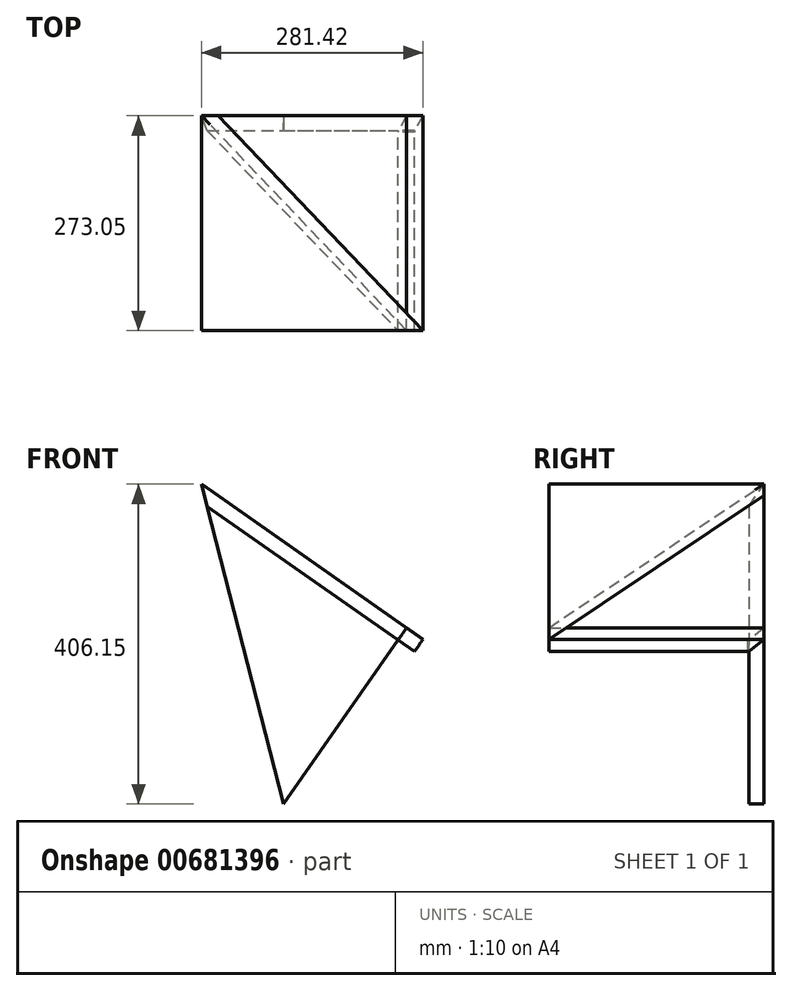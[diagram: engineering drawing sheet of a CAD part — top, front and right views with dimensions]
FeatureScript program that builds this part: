
annotation { "Feature Type Name" : "Feature", "Feature Type Description" : "" }
export const myFeature = defineFeature(function(context is Context, id is Id, definition is map)
    precondition{}
    {
        {
            var Q0;
            Q0=qCreatedBy(makeId("Front.planeOp"),FACE);
            var sketch = newSketch(context, id + "F0", { "sketchPlane" : qUnion([Q0])});
            skLineSegment(sketch, "E0", {"start": v(0, 0) * mm, "end": v(249.68, -174.83) * mm});
            skLineSegment(sketch, "E1", {"start": v(0, 0) * mm, "end": v(0, -53.72) * mm});
            skLineSegment(sketch, "E2", {"start": v(10.93, 15.6) * mm, "end": v(260.6, -159.22) * mm});
            skLineSegment(sketch, "E3", {"start": v(260.6, -159.22) * mm, "end": v(249.68, -174.83) * mm});
            skLineSegment(sketch, "E4", {"start": v(0, 0) * mm, "end": v(0, 29.97) * mm});
            skLineSegment(sketch, "E5", {"start": v(10.93, 15.6) * mm, "end": v(0, 23.26) * mm});
            skSolve(sketch);
        }
        {
            var Q0;
            Q0=makeQuery(id+"F0.imprint","IMPRINT",FACE,{"disambiguationData":[TD([[makeQuery(id+"F0.imprint","IMPRINT",EDGE,{"derivedFrom":sQuery(id+"F0.wireOp",EDGE,"E0")}),1.0]])]});
            extrude(context, id + "F1", {"entities" : qUnion([Q0]), "depth" : 273.05 * mm, "offsetDistance" : 25.4 * mm});
        }
        {
            var Q0;
            Q0=makeQuery(id+"F1.opExtrude","SWEPT_FACE",FACE,{"disambiguationData":[OSD([sQuery(id+"F0.wireOp",EDGE,"E2")])]});
            var sketch = newSketch(context, id + "F2", { "sketchPlane" : qUnion([Q0])});
            skPoint(sketch, "E6.startSnap0", {"position": v(304.8, -136.53) * mm});
            skLineSegment(sketch, "E7", {"start": v(304.8, 0) * mm, "end": v(304.8, 0) * mm});
            skLineSegment(sketch, "E8", {"start": v(304.8, -273.05) * mm, "end": v(-13.34, -273.05) * mm});
            skLineSegment(sketch, "E9", {"start": v(-13.34, -273.05) * mm, "end": v(-13.34, -88.9) * mm});
            skLineSegment(sketch, "E10", {"start": v(-13.34, -88.9) * mm, "end": v(-13.34, 0) * mm});
            skLineSegment(sketch, "E11", {"start": v(-13.34, 0) * mm, "end": v(304.8, -273.05) * mm});
            skSolve(sketch);
        }
        {
            var Q0;
            Q0 = qSketchRegion(id + "F2", true);
            extrude(context, id + "F3", {"entities" : qUnion([Q0]), "operationType" : NewBodyOperationType.REMOVE, "oppositeDirection" : true, "depth" : 25.4 * mm, "offsetDistance" : 25.4 * mm});
        }
        {
            var Q0;
            Q0=makeQuery(id+"F3.boolean.opBoolean","INTERSECT",EDGE,{"derivedFrom":[makeQuery(id+"F1.opExtrude","SWEPT_FACE",FACE,{"disambiguationData":[OSD([sQuery(id+"F0.wireOp",EDGE,"E0")])]}),makeQuery(id+"F3.opExtrude","SWEPT_FACE",FACE,{"disambiguationData":[OSD([sQuery(id+"F2.wireOp",EDGE,"XtUcBT52-hiCQ-KWcL-Mt3B-IRJ0phNK8BbC")])]})]});
            var Q1;
            Q1=makeQuery(id+"F3.boolean.opBoolean","INTERSECT",EDGE,{"derivedFrom":[makeQuery(id+"F1.opExtrude","SWEPT_FACE",FACE,{"disambiguationData":[OSD([sQuery(id+"F0.wireOp",EDGE,"E0")])]}),makeQuery(id+"F3.opExtrude","SWEPT_FACE",FACE,{"disambiguationData":[OSD([sQuery(id+"F2.wireOp",EDGE,"sxALio6w-iuIC-QzVB-jW2B-1LGJXtkoLwBy")])]})]});
            var Q2;
            Q2=makeQuery(id+"F1.opExtrude","CAP_EDGE",EDGE,{"disambiguationData":[OSD([sQuery(id+"F0.wireOp",EDGE,"E0")])],"isStart":true});
            chamfer(context, id + "F4", {"entities" : qUnion([Q0, Q1, Q2]), "width" : 19.05 * mm, "tangentPropagation" : true});
        }
        {
            var Q0;
            Q0=makeQuery(id+"F1.opExtrude","SWEPT_BODY",BODY,{"disambiguationData":[OSD([sQuery(id+"F0.wireOp",EDGE,"E0"),sQuery(id+"F0.wireOp",EDGE,"E2"),sQuery(id+"F0.wireOp",EDGE,"E3"),sQuery(id+"F0.wireOp",EDGE,"E4"),sQuery(id+"F0.wireOp",EDGE,"E5")])]});
            var Q1;
            Q1=makeQuery(id+"F4.opChamfer","BLEND_FACE",FACE,{"disambiguationData":[OSD([sQuery(id+"F0.wireOp",EDGE,"E0")])]});
            mirror(context, id + "F5", {"operationType" : NewBodyOperationType.ADD, "entities" : qUnion([Q0]), "mirrorPlane" : qUnion([Q1])});
        }
        {
            var Q0;
            {var subQ0=makeQuery(id+"F1.opExtrude","SWEPT_FACE",FACE,{"disambiguationData":[OSD([sQuery(id+"F0.wireOp",EDGE,"E3")])]});Q0=makeQuery(id+"F5.boolean.opBoolean","MERGE",FACE,{"derivedFrom":[subQ0,makeQuery(id+"F5.opPattern","COPY",FACE,{"derivedFrom":subQ0,"instanceName":"1"})]});}
            var sketch = newSketch(context, id + "F6", { "sketchPlane" : qUnion([Q0])});
            skLineSegment(sketch, "E12", {"start": v(-19.05, 0) * mm, "end": v(-19.05, -1.59) * mm});
            skLineSegment(sketch, "E13", {"start": v(-19.05, 0) * mm, "end": v(-20.64, 0) * mm});
            skLineSegment(sketch, "E14", {"start": v(-20.64, 0) * mm, "end": v(-20.64, -1.59) * mm});
            skLineSegment(sketch, "E15", {"start": v(-20.64, -1.59) * mm, "end": v(-19.05, -1.59) * mm});
            skSolve(sketch);
        }
        {
            var Q0;
            Q0=makeQuery(id+"F6.imprint","IMPRINT",FACE,{"disambiguationData":[TD([[makeQuery(id+"F6.imprint","IMPRINT",EDGE,{"derivedFrom":sQuery(id+"F6.wireOp",EDGE,"E12")}),1.0]])]});
            var Q1;
            Q1 = qSketchRegion(id + "F2", true);
            extrude(context, id + "F7", {"entities" : qUnion([Q0, Q1]), "depth" : 25.4 * mm, "offsetDistance" : 25.4 * mm});
        }
    });
